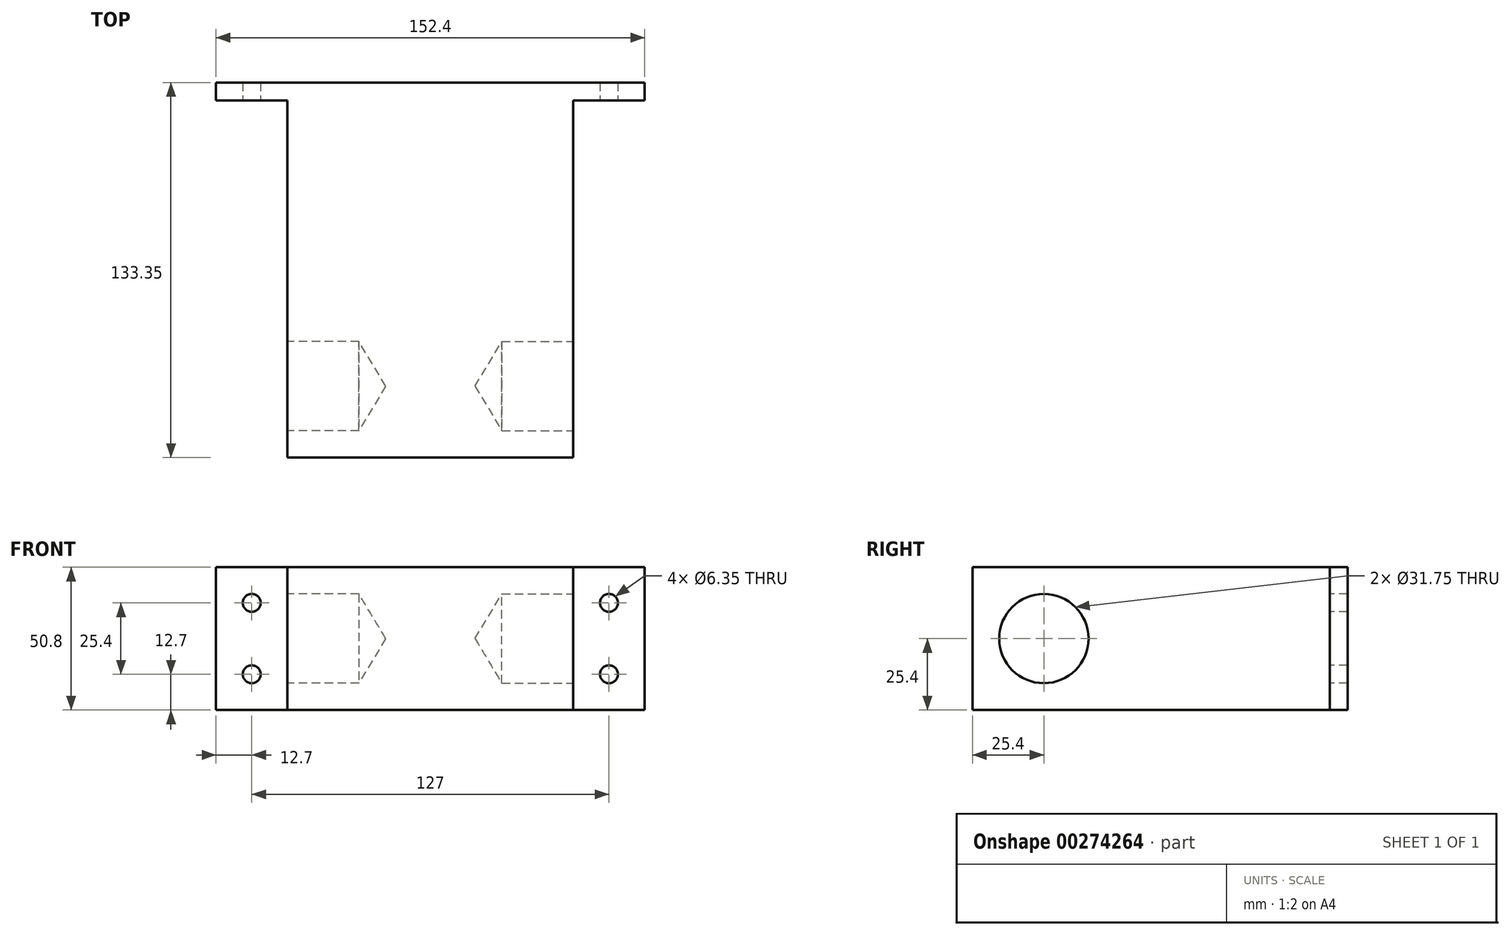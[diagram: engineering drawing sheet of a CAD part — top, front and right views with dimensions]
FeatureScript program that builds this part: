
annotation { "Feature Type Name" : "Feature", "Feature Type Description" : "" }
export const myFeature = defineFeature(function(context is Context, id is Id, definition is map)
    precondition{}
    {
        {
            var Q0;
            Q0=qCreatedBy(makeId("Front.planeOp"),FACE);
            var sketch = newSketch(context, id + "F0", { "sketchPlane" : qUnion([Q0])});
            skLineSegment(sketch, "E0.bottom", {"start": v(0, 0) * mm, "end": v(152.4, 0) * mm});
            skLineSegment(sketch, "E0.top", {"start": v(0, 50.8) * mm, "end": v(152.4, 50.8) * mm});
            skLineSegment(sketch, "E0.left", {"start": v(0, 0) * mm, "end": v(0, 50.8) * mm});
            skLineSegment(sketch, "E0.right", {"start": v(152.4, 0) * mm, "end": v(152.4, 50.8) * mm});
            skSolve(sketch);
        }
        {
            var Q0;
            Q0=makeQuery(id+"F0.imprint","IMPRINT",FACE,{"disambiguationData":[TD([[makeQuery(id+"F0.imprint","IMPRINT",EDGE,{"derivedFrom":sQuery(id+"F0.wireOp",EDGE,"E0.bottom")}),1.0]])]});
            extrude(context, id + "F1", {"entities" : qUnion([Q0]), "depth" : 6.35 * mm});
        }
        {
            var Q0;
            Q0=makeQuery(id+"F1.opExtrude","CAP_FACE",FACE,{"disambiguationData":[OSD([sQuery(id+"F0.wireOp",EDGE,"E0.bottom"),sQuery(id+"F0.wireOp",EDGE,"E0.top"),sQuery(id+"F0.wireOp",EDGE,"E0.left"),sQuery(id+"F0.wireOp",EDGE,"E0.right")])],"isStart":false});
            var sketch = newSketch(context, id + "F2", { "sketchPlane" : qUnion([Q0])});
            skPoint(sketch, "E1", {"position": v(12.7, 38.1) * mm});
            skPoint(sketch, "E2", {"position": v(12.7, 12.7) * mm});
            skPoint(sketch, "E3", {"position": v(139.7, 38.1) * mm});
            skPoint(sketch, "E4", {"position": v(139.7, 12.7) * mm});
            skSolve(sketch);
        }
        {
            var Q0;
            Q0=sQuery(id+"F2.wireOp",VERTEX,"E1");
            var Q1;
            Q1=sQuery(id+"F2.wireOp",VERTEX,"E2");
            var Q2;
            Q2=sQuery(id+"F2.wireOp",VERTEX,"E3");
            var Q3;
            Q3=sQuery(id+"F2.wireOp",VERTEX,"E4");
            var Q4;
            Q4=makeQuery(id+"F1.opExtrude","SWEPT_BODY",BODY,{"disambiguationData":[OSD([sQuery(id+"F0.wireOp",EDGE,"E0.bottom"),sQuery(id+"F0.wireOp",EDGE,"E0.top"),sQuery(id+"F0.wireOp",EDGE,"E0.left"),sQuery(id+"F0.wireOp",EDGE,"E0.right")])]});
            hole(context, id + "F3", {"style" : HoleStyle.SIMPLE, "endStyle" : HoleEndStyle.THROUGH, "holeDiameter" : 6.35 * mm, "tappedDepth" : 12.7 * mm, "tapClearance" : 3, "locations" : qUnion([Q0, Q1, Q2, Q3]), "scope" : qUnion([Q4])});
        }
        {
            var Q0;
            Q0=makeQuery(id+"F1.opExtrude","CAP_FACE",FACE,{"disambiguationData":[OSD([sQuery(id+"F0.wireOp",EDGE,"E0.bottom"),sQuery(id+"F0.wireOp",EDGE,"E0.top"),sQuery(id+"F0.wireOp",EDGE,"E0.left"),sQuery(id+"F0.wireOp",EDGE,"E0.right")])],"isStart":false});
            var sketch = newSketch(context, id + "F4", { "sketchPlane" : qUnion([Q0])});
            skLineSegment(sketch, "E5.bottom", {"start": v(25.4, 50.8) * mm, "end": v(127, 50.8) * mm});
            skLineSegment(sketch, "E5.top", {"start": v(25.4, 0) * mm, "end": v(127, 0) * mm});
            skLineSegment(sketch, "E5.left", {"start": v(25.4, 50.8) * mm, "end": v(25.4, 0) * mm});
            skLineSegment(sketch, "E5.right", {"start": v(127, 50.8) * mm, "end": v(127, 0) * mm});
            skSolve(sketch);
        }
        {
            var Q0;
            Q0=makeQuery(id+"F4.imprint","IMPRINT",FACE,{"disambiguationData":[TD([[makeQuery(id+"F4.imprint","IMPRINT",EDGE,{"derivedFrom":sQuery(id+"F4.wireOp",EDGE,"E5.bottom")}),-1.0]])]});
            extrude(context, id + "F5", {"entities" : qUnion([Q0]), "operationType" : NewBodyOperationType.ADD, "depth" : 127 * mm});
        }
        {
            var Q0;
            Q0=makeQuery(id+"F5.opExtrude","SWEPT_FACE",FACE,{"disambiguationData":[OSD([sQuery(id+"F4.wireOp",EDGE,"E5.right")])]});
            var sketch = newSketch(context, id + "F6", { "sketchPlane" : qUnion([Q0])});
            skPoint(sketch, "E6", {"position": v(-107.95, 25.4) * mm});
            skSolve(sketch);
        }
        {
            var Q0;
            Q0=sQuery(id+"F6.wireOp",VERTEX,"E6");
            var Q1;
            Q1=makeQuery(id+"F1.opExtrude","SWEPT_BODY",BODY,{"disambiguationData":[OSD([sQuery(id+"F0.wireOp",EDGE,"E0.bottom"),sQuery(id+"F0.wireOp",EDGE,"E0.top"),sQuery(id+"F0.wireOp",EDGE,"E0.left"),sQuery(id+"F0.wireOp",EDGE,"E0.right")])]});
            hole(context, id + "F7", {"style" : HoleStyle.SIMPLE, "endStyle" : HoleEndStyle.BLIND, "holeDiameter" : 31.75 * mm, "holeDepth" : 25.4 * mm, "tappedDepth" : 12.7 * mm, "tapClearance" : 3, "locations" : qUnion([Q0]), "scope" : qUnion([Q1])});
        }
        {
            var Q0;
            Q0=makeQuery(id+"F5.opExtrude","SWEPT_FACE",FACE,{"disambiguationData":[OSD([sQuery(id+"F4.wireOp",EDGE,"E5.left")])]});
            var sketch = newSketch(context, id + "F8", { "sketchPlane" : qUnion([Q0])});
            skPoint(sketch, "E7", {"position": v(107.95, 25.4) * mm});
            skSolve(sketch);
        }
        {
            var Q0;
            Q0=sQuery(id+"F8.wireOp",VERTEX,"E7");
            var Q1;
            Q1=makeQuery(id+"F1.opExtrude","SWEPT_BODY",BODY,{"disambiguationData":[OSD([sQuery(id+"F0.wireOp",EDGE,"E0.bottom"),sQuery(id+"F0.wireOp",EDGE,"E0.top"),sQuery(id+"F0.wireOp",EDGE,"E0.left"),sQuery(id+"F0.wireOp",EDGE,"E0.right")])]});
            hole(context, id + "F9", {"style" : HoleStyle.SIMPLE, "endStyle" : HoleEndStyle.BLIND, "holeDiameter" : 31.75 * mm, "holeDepth" : 25.4 * mm, "tappedDepth" : 12.7 * mm, "tapClearance" : 3, "locations" : qUnion([Q0]), "scope" : qUnion([Q1])});
        }
    });
